# Revit family: FS_Скамейка_Лотос_R16
name_source: partatom
category: Антураж
revit_build: Autodesk Revit 2016 (Build: 20160314_0715(x64)
units: mm (PartAtom-declared; Revit-internal decimal feet)

## family parameters
Всегда вертикально = Да
Источник визуального образа = Геометрия семейства
На основе рабочей плоскости = Нет
Общий = Нет
При загрузке вырезать с полостями = Нет
Точка расчета площади = Нет

## types (6) — shared parameters
ADSK_Код изделия = 8346
ADSK_Материал доски = Орех
ADSK_Материал крепления = Цинк
ADSK_Материал опоры = Чугун, ковкий
ADSK_Размер_Высота = 868 мм
ADSK_Размер_Ширина = 768 мм
URL = https://hobbyka.ru
Изготовитель = ООО 'Хоббика'
Комментарии к типоразмеру = Материалы: сталь, брус
zero-valued in all types: Высота

## per-type parameters (varying)
| type | ADSK_Наименование | ADSK_Размер_Длина | Стоимость | Третья опора |
| Скамейка кованая «Лотос» 2.0м | Скамейка кованая «Лотос» 2.0м | 2000 мм | 14333 $ | Да |
| Скамейка кованая «Лотос» 0.6м | Скамейка кованая «Лотос» 0.6 м | 600 мм | 7718 $ | Нет |
| Скамейка кованая «Лотос» 3.0м | Скамейка кованая «Лотос» 3.0м | 3000 мм | 15333 $ | Да |
| Скамейка кованая «Лотос» 1.5м | Скамейка кованая «Лотос» 1.5м | 1500 мм | 8820 $ | Нет |
| Скамейка кованая «Лотос» 1.2м | Скамейка кованая «Лотос» 1.2м | 1200 мм | 8269 $ | Нет |
| Скамейка кованая «Лотос» 1.8м | Скамейка кованая «Лотос» 1.8м | 1800 мм | 9482 $ | Нет |
